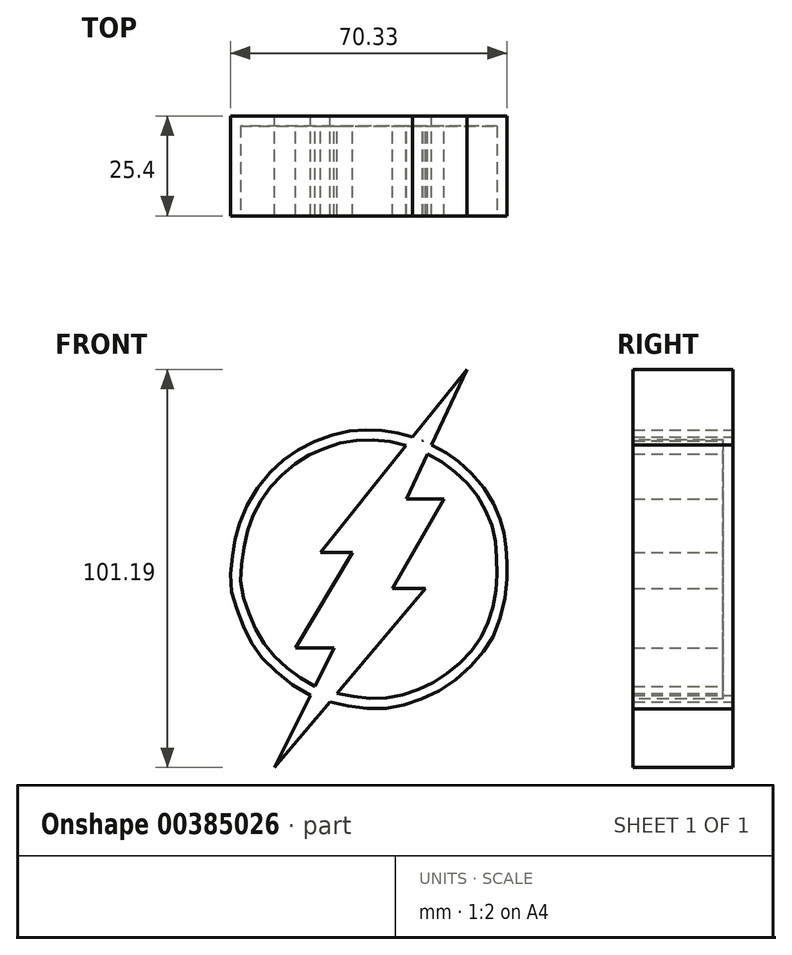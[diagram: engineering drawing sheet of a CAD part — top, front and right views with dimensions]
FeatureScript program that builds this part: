
annotation { "Feature Type Name" : "Feature", "Feature Type Description" : "" }
export const myFeature = defineFeature(function(context is Context, id is Id, definition is map)
    precondition{}
    {
        {
            var Q0;
            Q0=qCreatedBy(makeId("Front.planeOp"),FACE);
            var sketch = newSketch(context, id + "F0", { "sketchPlane" : qUnion([Q0])});
            skFitSpline(sketch, "E0", {"points": [v(6.83, 50.56) * mm, v(0.98, 52) * mm, v(-5.5, 52.4) * mm, v(-12.47, 51.36) * mm, v(-20.8, 48.08) * mm, v(-27.05, 43.67) * mm, v(-33.38, 36.39) * mm, v(-37.38, 27.82) * mm, v(-38.74, 21.09) * mm, v(-39.33, 13.17) * mm, v(-37.18, 5.24) * mm, v(-33.67, -2.35) * mm, v(-27.78, -9.03) * mm, v(-18.83, -15.15) * mm, v(-10.56, -17.52) * mm, v(-1.16, -18.43) * mm, v(7.45, -16.62) * mm, v(15.83, -12.54) * mm, v(23.76, -5.4) * mm, v(28.06, 1.5) * mm, v(30.74, 12.18) * mm, v(30.84, 19.13) * mm, v(30.36, 25.23) * mm, v(28.84, 30.47) * mm, v(25.1, 37.6) * mm, v(18.99, 43.95) * mm, v(14.12, 47.35) * mm, v(6.83, 50.56) * mm]});
            skLineSegment(sketch, "E1", {"start": v(20.68, 67.76) * mm, "end": v(-16.47, 21.2) * mm});
            skLineSegment(sketch, "E2", {"start": v(-16.47, 21.2) * mm, "end": v(-8.32, 21.2) * mm});
            skLineSegment(sketch, "E3", {"start": v(-8.32, 21.2) * mm, "end": v(-22.83, -3) * mm});
            skLineSegment(sketch, "E4", {"start": v(-22.83, -3) * mm, "end": v(-13.06, -3) * mm});
            skLineSegment(sketch, "E5", {"start": v(-13.06, -3) * mm, "end": v(-28.16, -33.43) * mm});
            skLineSegment(sketch, "E6", {"start": v(-28.16, -33.43) * mm, "end": v(10.23, 12.1) * mm});
            skLineSegment(sketch, "E7", {"start": v(10.23, 12.1) * mm, "end": v(1.74, 12.1) * mm});
            skLineSegment(sketch, "E8", {"start": v(1.74, 12.1) * mm, "end": v(14.93, 34.84) * mm});
            skLineSegment(sketch, "E9", {"start": v(14.93, 34.84) * mm, "end": v(5.42, 34.84) * mm});
            skLineSegment(sketch, "E10", {"start": v(5.42, 34.84) * mm, "end": v(20.68, 67.76) * mm});
            skSolve(sketch);
        }
        {
            var Q0;
            Q0 = qSketchRegion(id + "F0", true);
            extrude(context, id + "F1", {"entities" : qUnion([Q0]), "depth" : 25.4 * mm});
        }
        {
            var Q0;
            Q0=makeQuery(id+"F1.opExtrude","CAP_FACE",FACE,{"disambiguationData":[OSD([sQuery(id+"F0.wireOp",EDGE,"E0"),sQuery(id+"F0.wireOp",EDGE,"E1"),sQuery(id+"F0.wireOp",EDGE,"E5"),sQuery(id+"F0.wireOp",EDGE,"E6"),sQuery(id+"F0.wireOp",EDGE,"E10")])],"isStart":false});
            shell(context, id + "F2", {"entities" : qUnion([Q0]), "thickness" : 2.54 * mm});
        }
        {
            var Q0;
            {var subQ7=sQuery(id+"F0.wireOp",EDGE,"E2");Q0=makeQuery(id+"F0.imprint","IMPRINT",FACE,{"disambiguationData":[TD([[makeQuery(id+"F0.imprint","IMPRINT",EDGE,{"derivedFrom":subQ7}),1.0]])]});}
            extrude(context, id + "F3", {"entities" : qUnion([Q0]), "operationType" : NewBodyOperationType.ADD, "depth" : 25.4 * mm});
        }
    });
